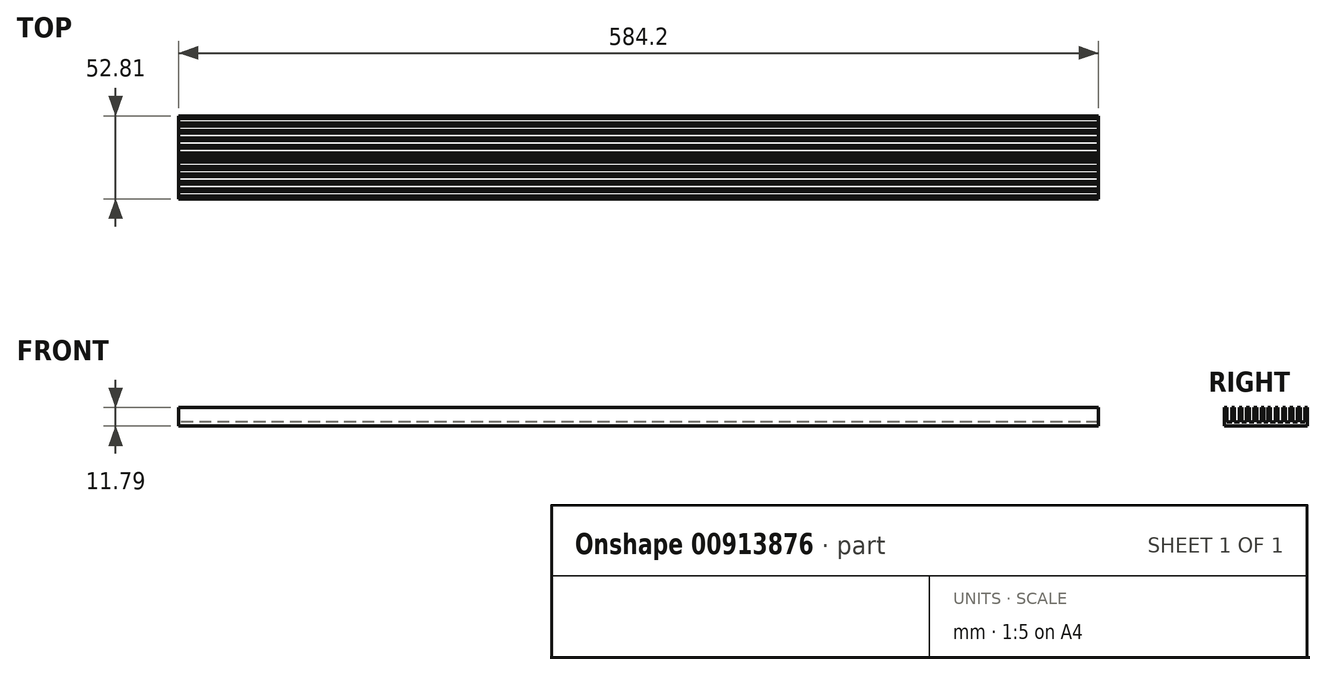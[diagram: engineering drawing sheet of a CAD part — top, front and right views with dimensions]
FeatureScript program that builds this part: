
annotation { "Feature Type Name" : "Feature", "Feature Type Description" : "" }
export const myFeature = defineFeature(function(context is Context, id is Id, definition is map)
    precondition{}
    {
        {
            var Q0;
            Q0=qCreatedBy(makeId("Right.planeOp"),FACE);
            var sketch = newSketch(context, id + "F0", { "sketchPlane" : qUnion([Q0])});
            skLineSegment(sketch, "E0.bottom", {"start": v(-26.79, 1.1) * mm, "end": v(-25.09, 1.1) * mm});
            skLineSegment(sketch, "E0.top", {"start": v(-26.79, -10.69) * mm, "end": v(26.02, -10.69) * mm});
            skLineSegment(sketch, "E0.left", {"start": v(-26.79, 1.1) * mm, "end": v(-26.79, -10.69) * mm});
            skLineSegment(sketch, "E0.right", {"start": v(26.02, 1.1) * mm, "end": v(26.02, -10.69) * mm});
            skLineSegment(sketch, "E1.0", {"start": v(-25.09, -8.2) * mm, "end": v(-22.1, -8.2) * mm});
            skLineSegment(sketch, "E2.0", {"start": v(-25.09, 1.1) * mm, "end": v(-25.09, -8.2) * mm});
            skLineSegment(sketch, "E3.0", {"start": v(-22.1, 1.1) * mm, "end": v(-22.1, -8.2) * mm});
            skLineSegment(sketch, "E4.0", {"start": v(-20.39, 1.1) * mm, "end": v(-20.39, -8.2) * mm});
            skLineSegment(sketch, "E5.0", {"start": v(-17.4, 1.1) * mm, "end": v(-17.4, -8.2) * mm});
            skLineSegment(sketch, "E6.0", {"start": v(-15.7, 1.1) * mm, "end": v(-15.7, -8.2) * mm});
            skLineSegment(sketch, "E7.0", {"start": v(-12.7, 1.1) * mm, "end": v(-12.7, -8.2) * mm});
            skLineSegment(sketch, "E8.0", {"start": v(-11, 1.1) * mm, "end": v(-11, -8.2) * mm});
            skLineSegment(sketch, "E9.0", {"start": v(-8, 1.1) * mm, "end": v(-8, -8.2) * mm});
            skLineSegment(sketch, "E10.0", {"start": v(-6.3, 1.1) * mm, "end": v(-6.3, -8.2) * mm});
            skLineSegment(sketch, "E11.0", {"start": v(-3.3, 1.1) * mm, "end": v(-3.3, -8.2) * mm});
            skLineSegment(sketch, "E12.0", {"start": v(-1.6, 1.1) * mm, "end": v(-1.6, -8.2) * mm});
            skLineSegment(sketch, "E13.MirrorCS", {"start": v(0.82, 1.1) * mm, "end": v(0.82, -8.2) * mm});
            skLineSegment(sketch, "E14.MirrorCS", {"start": v(2.52, 1.1) * mm, "end": v(2.52, -8.2) * mm});
            skLineSegment(sketch, "E15.MirrorCS", {"start": v(5.52, 1.1) * mm, "end": v(5.52, -8.2) * mm});
            skLineSegment(sketch, "E16.MirrorCS", {"start": v(7.22, 1.1) * mm, "end": v(7.22, -8.2) * mm});
            skLineSegment(sketch, "E17.MirrorCS", {"start": v(10.22, 1.1) * mm, "end": v(10.22, -8.2) * mm});
            skLineSegment(sketch, "E18.MirrorCS", {"start": v(11.92, 1.1) * mm, "end": v(11.92, -8.2) * mm});
            skLineSegment(sketch, "E19.MirrorCS", {"start": v(14.92, 1.1) * mm, "end": v(14.92, -8.2) * mm});
            skLineSegment(sketch, "E20.MirrorCS", {"start": v(16.62, 1.1) * mm, "end": v(16.62, -8.2) * mm});
            skLineSegment(sketch, "E21.MirrorCS", {"start": v(19.62, 1.1) * mm, "end": v(19.62, -8.2) * mm});
            skLineSegment(sketch, "E22.MirrorCS", {"start": v(21.32, 1.1) * mm, "end": v(21.32, -8.2) * mm});
            skLineSegment(sketch, "E23.MirrorCS", {"start": v(24.31, 1.1) * mm, "end": v(24.31, -8.2) * mm});
            skLineSegment(sketch, "E24.trimOffspring", {"start": v(-22.1, 1.1) * mm, "end": v(-20.39, 1.1) * mm});
            skLineSegment(sketch, "E25.trimOffspring", {"start": v(-17.4, 1.1) * mm, "end": v(-15.7, 1.1) * mm});
            skLineSegment(sketch, "E26.trimOffspring", {"start": v(-12.7, 1.1) * mm, "end": v(-11, 1.1) * mm});
            skLineSegment(sketch, "E27.trimOffspring", {"start": v(-8, 1.1) * mm, "end": v(-6.3, 1.1) * mm});
            skLineSegment(sketch, "E28.trimOffspring", {"start": v(-3.3, 1.1) * mm, "end": v(-1.6, 1.1) * mm});
            skLineSegment(sketch, "E29.trimOffspring", {"start": v(0.82, 1.1) * mm, "end": v(2.52, 1.1) * mm});
            skLineSegment(sketch, "E30.trimOffspring", {"start": v(5.52, 1.1) * mm, "end": v(7.22, 1.1) * mm});
            skLineSegment(sketch, "E31.trimOffspring", {"start": v(10.22, 1.1) * mm, "end": v(11.92, 1.1) * mm});
            skLineSegment(sketch, "E32.trimOffspring", {"start": v(14.92, 1.1) * mm, "end": v(16.62, 1.1) * mm});
            skLineSegment(sketch, "E33.trimOffspring", {"start": v(19.62, 1.1) * mm, "end": v(21.32, 1.1) * mm});
            skLineSegment(sketch, "E34.trimOffspring", {"start": v(24.31, 1.1) * mm, "end": v(26.02, 1.1) * mm});
            skLineSegment(sketch, "E35.trimOffspring", {"start": v(16.62, -8.2) * mm, "end": v(19.62, -8.2) * mm});
            skLineSegment(sketch, "E36.trimOffspring", {"start": v(21.32, -8.2) * mm, "end": v(24.31, -8.2) * mm});
            skLineSegment(sketch, "E37.trimOffspring", {"start": v(11.92, -8.2) * mm, "end": v(14.92, -8.2) * mm});
            skLineSegment(sketch, "E38.trimOffspring", {"start": v(7.22, -8.2) * mm, "end": v(10.22, -8.2) * mm});
            skLineSegment(sketch, "E39.trimOffspring", {"start": v(2.52, -8.2) * mm, "end": v(5.52, -8.2) * mm});
            skLineSegment(sketch, "E40.trimOffspring", {"start": v(-1.6, -8.2) * mm, "end": v(0.82, -8.2) * mm});
            skLineSegment(sketch, "E41.trimOffspring", {"start": v(-6.3, -8.2) * mm, "end": v(-3.3, -8.2) * mm});
            skLineSegment(sketch, "E42.trimOffspring", {"start": v(-11, -8.2) * mm, "end": v(-8, -8.2) * mm});
            skLineSegment(sketch, "E43.trimOffspring", {"start": v(-15.7, -8.2) * mm, "end": v(-12.7, -8.2) * mm});
            skLineSegment(sketch, "E44.trimOffspring", {"start": v(-20.39, -8.2) * mm, "end": v(-17.4, -8.2) * mm});
            skSolve(sketch);
        }
        {
            var Q0;
            Q0=makeQuery(id+"F0.imprint","IMPRINT",FACE,{"disambiguationData":[TD([[makeQuery(id+"F0.imprint","IMPRINT",EDGE,{"derivedFrom":sQuery(id+"F0.wireOp",EDGE,"E0.bottom")}),-1.0]])]});
            extrude(context, id + "F1", {"entities" : qUnion([Q0]), "depth" : 584.2 * mm, "offsetDistance" : 25.4 * mm});
        }
    });
